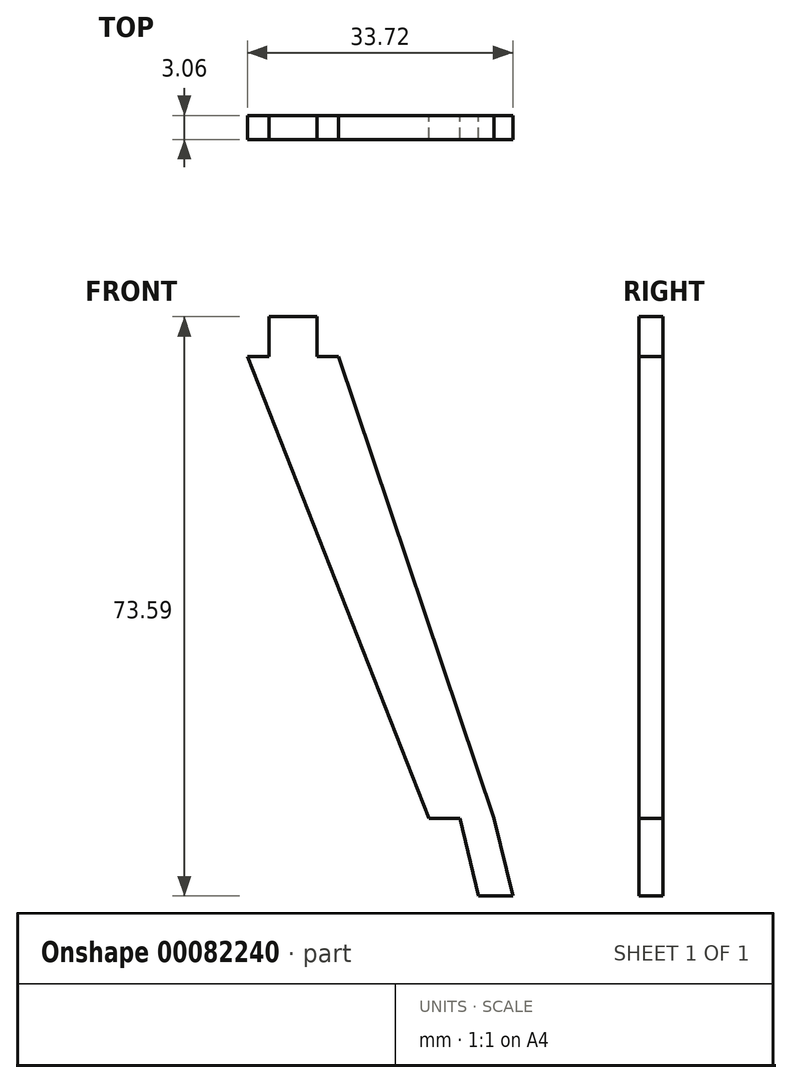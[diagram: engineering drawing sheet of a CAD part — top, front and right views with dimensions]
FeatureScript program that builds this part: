
annotation { "Feature Type Name" : "Feature", "Feature Type Description" : "" }
export const myFeature = defineFeature(function(context is Context, id is Id, definition is map)
    precondition{}
    {
        {
            var Q0;
            Q0=qCreatedBy(makeId("Front.planeOp"),FACE);
            var sketch = newSketch(context, id + "F0", { "sketchPlane" : qUnion([Q0])});
            skLineSegment(sketch, "E0", {"start": v(-60.74, -18.2) * mm, "end": v(-58.35, -28.08) * mm});
            skLineSegment(sketch, "E1", {"start": v(-58.35, -28.08) * mm, "end": v(-54.01, -28.08) * mm});
            skLineSegment(sketch, "E2", {"start": v(-54.01, -28.08) * mm, "end": v(-56.4, -18.2) * mm});
            skLineSegment(sketch, "E3", {"start": v(-76.15, 40.43) * mm, "end": v(-87.73, 40.43) * mm});
            skLineSegment(sketch, "E4", {"start": v(-85, 40.43) * mm, "end": v(-85, 45.5) * mm});
            skLineSegment(sketch, "E5", {"start": v(-85, 45.5) * mm, "end": v(-78.9, 45.5) * mm});
            skLineSegment(sketch, "E6", {"start": v(-78.9, 45.5) * mm, "end": v(-78.9, 40.43) * mm});
            skLineSegment(sketch, "E7", {"start": v(-56.4, -18.2) * mm, "end": v(-76.15, 40.43) * mm});
            skLineSegment(sketch, "E8", {"start": v(-60.74, -18.2) * mm, "end": v(-64.68, -18.2) * mm});
            skLineSegment(sketch, "E9", {"start": v(-64.68, -18.2) * mm, "end": v(-87.73, 40.43) * mm});
            skSolve(sketch);
        }
        {
            var Q0;
            Q0 = qSketchRegion(id + "F0", true);
            extrude(context, id + "F1", {"entities" : qUnion([Q0]), "depth" : 3.06 * mm});
        }
    });
